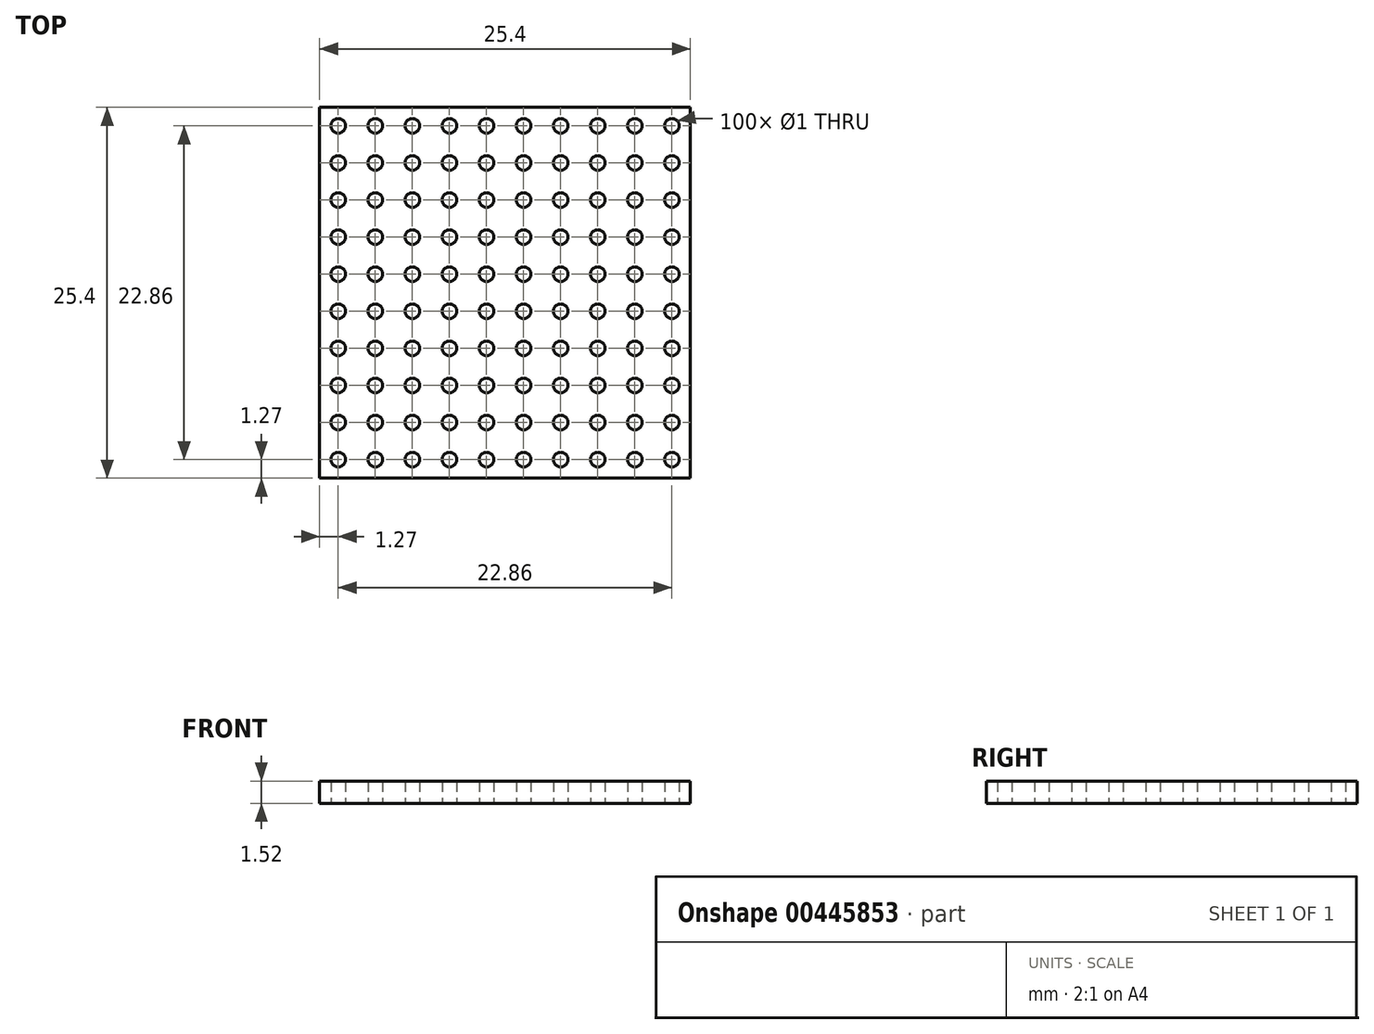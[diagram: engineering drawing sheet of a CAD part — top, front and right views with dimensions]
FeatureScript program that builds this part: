
annotation { "Feature Type Name" : "Feature", "Feature Type Description" : "" }
export const myFeature = defineFeature(function(context is Context, id is Id, definition is map)
    precondition{}
    {
        {
            var Q0;
            Q0=qCreatedBy(makeId("Top.planeOp"),FACE);
            var sketch = newSketch(context, id + "F0", { "sketchPlane" : qUnion([Q0])});
            skCircle(sketch, "E0", {"center": v(0, 0) * mm, "radius": 0.5 * mm});
            skCircle(sketch, "E1.0.1.0", {"center": v(0, 2.54) * mm, "radius": 0.5 * mm});
            skCircle(sketch, "E1.0.2.0", {"center": v(0, 5.08) * mm, "radius": 0.5 * mm});
            skCircle(sketch, "E1.0.3.0", {"center": v(0, 7.62) * mm, "radius": 0.5 * mm});
            skCircle(sketch, "E1.0.4.0", {"center": v(0, 10.16) * mm, "radius": 0.5 * mm});
            skCircle(sketch, "E1.0.5.0", {"center": v(0, 12.7) * mm, "radius": 0.5 * mm});
            skCircle(sketch, "E1.0.6.0", {"center": v(0, 15.24) * mm, "radius": 0.5 * mm});
            skCircle(sketch, "E1.0.7.0", {"center": v(0, 17.78) * mm, "radius": 0.5 * mm});
            skCircle(sketch, "E1.0.8.0", {"center": v(0, 20.32) * mm, "radius": 0.5 * mm});
            skCircle(sketch, "E1.0.9.0", {"center": v(0, 22.86) * mm, "radius": 0.5 * mm});
            skCircle(sketch, "E1.1.0.0", {"center": v(2.54, 0) * mm, "radius": 0.5 * mm});
            skCircle(sketch, "E1.1.1.0", {"center": v(2.54, 2.54) * mm, "radius": 0.5 * mm});
            skCircle(sketch, "E1.1.2.0", {"center": v(2.54, 5.08) * mm, "radius": 0.5 * mm});
            skCircle(sketch, "E1.1.3.0", {"center": v(2.54, 7.62) * mm, "radius": 0.5 * mm});
            skCircle(sketch, "E1.1.4.0", {"center": v(2.54, 10.16) * mm, "radius": 0.5 * mm});
            skCircle(sketch, "E1.1.5.0", {"center": v(2.54, 12.7) * mm, "radius": 0.5 * mm});
            skCircle(sketch, "E1.1.6.0", {"center": v(2.54, 15.24) * mm, "radius": 0.5 * mm});
            skCircle(sketch, "E1.1.7.0", {"center": v(2.54, 17.78) * mm, "radius": 0.5 * mm});
            skCircle(sketch, "E1.1.8.0", {"center": v(2.54, 20.32) * mm, "radius": 0.5 * mm});
            skCircle(sketch, "E1.1.9.0", {"center": v(2.54, 22.86) * mm, "radius": 0.5 * mm});
            skCircle(sketch, "E1.2.0.0", {"center": v(5.08, 0) * mm, "radius": 0.5 * mm});
            skCircle(sketch, "E1.2.1.0", {"center": v(5.08, 2.54) * mm, "radius": 0.5 * mm});
            skCircle(sketch, "E1.2.2.0", {"center": v(5.08, 5.08) * mm, "radius": 0.5 * mm});
            skCircle(sketch, "E1.2.3.0", {"center": v(5.08, 7.62) * mm, "radius": 0.5 * mm});
            skCircle(sketch, "E1.2.4.0", {"center": v(5.08, 10.16) * mm, "radius": 0.5 * mm});
            skCircle(sketch, "E1.2.5.0", {"center": v(5.08, 12.7) * mm, "radius": 0.5 * mm});
            skCircle(sketch, "E1.2.6.0", {"center": v(5.08, 15.24) * mm, "radius": 0.5 * mm});
            skCircle(sketch, "E1.2.7.0", {"center": v(5.08, 17.78) * mm, "radius": 0.5 * mm});
            skCircle(sketch, "E1.2.8.0", {"center": v(5.08, 20.32) * mm, "radius": 0.5 * mm});
            skCircle(sketch, "E1.2.9.0", {"center": v(5.08, 22.86) * mm, "radius": 0.5 * mm});
            skCircle(sketch, "E1.3.0.0", {"center": v(7.62, 0) * mm, "radius": 0.5 * mm});
            skCircle(sketch, "E1.3.1.0", {"center": v(7.62, 2.54) * mm, "radius": 0.5 * mm});
            skCircle(sketch, "E1.3.2.0", {"center": v(7.62, 5.08) * mm, "radius": 0.5 * mm});
            skCircle(sketch, "E1.3.3.0", {"center": v(7.62, 7.62) * mm, "radius": 0.5 * mm});
            skCircle(sketch, "E1.3.4.0", {"center": v(7.62, 10.16) * mm, "radius": 0.5 * mm});
            skCircle(sketch, "E1.3.5.0", {"center": v(7.62, 12.7) * mm, "radius": 0.5 * mm});
            skCircle(sketch, "E1.3.6.0", {"center": v(7.62, 15.24) * mm, "radius": 0.5 * mm});
            skCircle(sketch, "E1.3.7.0", {"center": v(7.62, 17.78) * mm, "radius": 0.5 * mm});
            skCircle(sketch, "E1.3.8.0", {"center": v(7.62, 20.32) * mm, "radius": 0.5 * mm});
            skCircle(sketch, "E1.3.9.0", {"center": v(7.62, 22.86) * mm, "radius": 0.5 * mm});
            skCircle(sketch, "E1.4.0.0", {"center": v(10.16, 0) * mm, "radius": 0.5 * mm});
            skCircle(sketch, "E1.4.1.0", {"center": v(10.16, 2.54) * mm, "radius": 0.5 * mm});
            skCircle(sketch, "E1.4.2.0", {"center": v(10.16, 5.08) * mm, "radius": 0.5 * mm});
            skCircle(sketch, "E1.4.3.0", {"center": v(10.16, 7.62) * mm, "radius": 0.5 * mm});
            skCircle(sketch, "E1.4.4.0", {"center": v(10.16, 10.16) * mm, "radius": 0.5 * mm});
            skCircle(sketch, "E1.4.5.0", {"center": v(10.16, 12.7) * mm, "radius": 0.5 * mm});
            skCircle(sketch, "E1.4.6.0", {"center": v(10.16, 15.24) * mm, "radius": 0.5 * mm});
            skCircle(sketch, "E1.4.7.0", {"center": v(10.16, 17.78) * mm, "radius": 0.5 * mm});
            skCircle(sketch, "E1.4.8.0", {"center": v(10.16, 20.32) * mm, "radius": 0.5 * mm});
            skCircle(sketch, "E1.4.9.0", {"center": v(10.16, 22.86) * mm, "radius": 0.5 * mm});
            skCircle(sketch, "E1.5.0.0", {"center": v(12.7, 0) * mm, "radius": 0.5 * mm});
            skCircle(sketch, "E1.5.1.0", {"center": v(12.7, 2.54) * mm, "radius": 0.5 * mm});
            skCircle(sketch, "E1.5.2.0", {"center": v(12.7, 5.08) * mm, "radius": 0.5 * mm});
            skCircle(sketch, "E1.5.3.0", {"center": v(12.7, 7.62) * mm, "radius": 0.5 * mm});
            skCircle(sketch, "E1.5.4.0", {"center": v(12.7, 10.16) * mm, "radius": 0.5 * mm});
            skCircle(sketch, "E1.5.5.0", {"center": v(12.7, 12.7) * mm, "radius": 0.5 * mm});
            skCircle(sketch, "E1.5.6.0", {"center": v(12.7, 15.24) * mm, "radius": 0.5 * mm});
            skCircle(sketch, "E1.5.7.0", {"center": v(12.7, 17.78) * mm, "radius": 0.5 * mm});
            skCircle(sketch, "E1.5.8.0", {"center": v(12.7, 20.32) * mm, "radius": 0.5 * mm});
            skCircle(sketch, "E1.5.9.0", {"center": v(12.7, 22.86) * mm, "radius": 0.5 * mm});
            skCircle(sketch, "E1.6.0.0", {"center": v(15.24, 0) * mm, "radius": 0.5 * mm});
            skCircle(sketch, "E1.6.1.0", {"center": v(15.24, 2.54) * mm, "radius": 0.5 * mm});
            skCircle(sketch, "E1.6.2.0", {"center": v(15.24, 5.08) * mm, "radius": 0.5 * mm});
            skCircle(sketch, "E1.6.3.0", {"center": v(15.24, 7.62) * mm, "radius": 0.5 * mm});
            skCircle(sketch, "E1.6.4.0", {"center": v(15.24, 10.16) * mm, "radius": 0.5 * mm});
            skCircle(sketch, "E1.6.5.0", {"center": v(15.24, 12.7) * mm, "radius": 0.5 * mm});
            skCircle(sketch, "E1.6.6.0", {"center": v(15.24, 15.24) * mm, "radius": 0.5 * mm});
            skCircle(sketch, "E1.6.7.0", {"center": v(15.24, 17.78) * mm, "radius": 0.5 * mm});
            skCircle(sketch, "E1.6.8.0", {"center": v(15.24, 20.32) * mm, "radius": 0.5 * mm});
            skCircle(sketch, "E1.6.9.0", {"center": v(15.24, 22.86) * mm, "radius": 0.5 * mm});
            skCircle(sketch, "E1.7.0.0", {"center": v(17.78, 0) * mm, "radius": 0.5 * mm});
            skCircle(sketch, "E1.7.1.0", {"center": v(17.78, 2.54) * mm, "radius": 0.5 * mm});
            skCircle(sketch, "E1.7.2.0", {"center": v(17.78, 5.08) * mm, "radius": 0.5 * mm});
            skCircle(sketch, "E1.7.3.0", {"center": v(17.78, 7.62) * mm, "radius": 0.5 * mm});
            skCircle(sketch, "E1.7.4.0", {"center": v(17.78, 10.16) * mm, "radius": 0.5 * mm});
            skCircle(sketch, "E1.7.5.0", {"center": v(17.78, 12.7) * mm, "radius": 0.5 * mm});
            skCircle(sketch, "E1.7.6.0", {"center": v(17.78, 15.24) * mm, "radius": 0.5 * mm});
            skCircle(sketch, "E1.7.7.0", {"center": v(17.78, 17.78) * mm, "radius": 0.5 * mm});
            skCircle(sketch, "E1.7.8.0", {"center": v(17.78, 20.32) * mm, "radius": 0.5 * mm});
            skCircle(sketch, "E1.7.9.0", {"center": v(17.78, 22.86) * mm, "radius": 0.5 * mm});
            skCircle(sketch, "E1.8.0.0", {"center": v(20.32, 0) * mm, "radius": 0.5 * mm});
            skCircle(sketch, "E1.8.1.0", {"center": v(20.32, 2.54) * mm, "radius": 0.5 * mm});
            skCircle(sketch, "E1.8.2.0", {"center": v(20.32, 5.08) * mm, "radius": 0.5 * mm});
            skCircle(sketch, "E1.8.3.0", {"center": v(20.32, 7.62) * mm, "radius": 0.5 * mm});
            skCircle(sketch, "E1.8.4.0", {"center": v(20.32, 10.16) * mm, "radius": 0.5 * mm});
            skCircle(sketch, "E1.8.5.0", {"center": v(20.32, 12.7) * mm, "radius": 0.5 * mm});
            skCircle(sketch, "E1.8.6.0", {"center": v(20.32, 15.24) * mm, "radius": 0.5 * mm});
            skCircle(sketch, "E1.8.7.0", {"center": v(20.32, 17.78) * mm, "radius": 0.5 * mm});
            skCircle(sketch, "E1.8.8.0", {"center": v(20.32, 20.32) * mm, "radius": 0.5 * mm});
            skCircle(sketch, "E1.8.9.0", {"center": v(20.32, 22.86) * mm, "radius": 0.5 * mm});
            skCircle(sketch, "E1.9.0.0", {"center": v(22.86, 0) * mm, "radius": 0.5 * mm});
            skCircle(sketch, "E1.9.1.0", {"center": v(22.86, 2.54) * mm, "radius": 0.5 * mm});
            skCircle(sketch, "E1.9.2.0", {"center": v(22.86, 5.08) * mm, "radius": 0.5 * mm});
            skCircle(sketch, "E1.9.3.0", {"center": v(22.86, 7.62) * mm, "radius": 0.5 * mm});
            skCircle(sketch, "E1.9.4.0", {"center": v(22.86, 10.16) * mm, "radius": 0.5 * mm});
            skCircle(sketch, "E1.9.5.0", {"center": v(22.86, 12.7) * mm, "radius": 0.5 * mm});
            skCircle(sketch, "E1.9.6.0", {"center": v(22.86, 15.24) * mm, "radius": 0.5 * mm});
            skCircle(sketch, "E1.9.7.0", {"center": v(22.86, 17.78) * mm, "radius": 0.5 * mm});
            skCircle(sketch, "E1.9.8.0", {"center": v(22.86, 20.32) * mm, "radius": 0.5 * mm});
            skCircle(sketch, "E1.9.9.0", {"center": v(22.86, 22.86) * mm, "radius": 0.5 * mm});
            skLineSegment(sketch, "E1.direction1", {"start": v(0, 0) * mm, "end": v(2.54, 0) * mm, "construction": true});
            skLineSegment(sketch, "E1.direction2", {"start": v(0, 0) * mm, "end": v(0, 2.54) * mm, "construction": true});
            skLineSegment(sketch, "E2.bottom", {"start": v(-1.27, -1.27) * mm, "end": v(24.13, -1.27) * mm});
            skLineSegment(sketch, "E2.top", {"start": v(-1.27, 24.13) * mm, "end": v(24.13, 24.13) * mm});
            skLineSegment(sketch, "E2.left", {"start": v(-1.27, -1.27) * mm, "end": v(-1.27, 24.13) * mm});
            skLineSegment(sketch, "E2.right", {"start": v(24.13, -1.27) * mm, "end": v(24.13, 24.13) * mm});
            skSolve(sketch);
        }
        {
            var Q0;
            Q0=makeQuery(id+"F0.imprint","IMPRINT",FACE,{"disambiguationData":[TD([[makeQuery(id+"F0.imprint","IMPRINT",EDGE,{"derivedFrom":sQuery(id+"F0.wireOp",EDGE,"E0")}),-1.0]])]});
            extrude(context, id + "F1", {"entities" : qUnion([Q0]), "depth" : 1.52 * mm});
        }
    });
